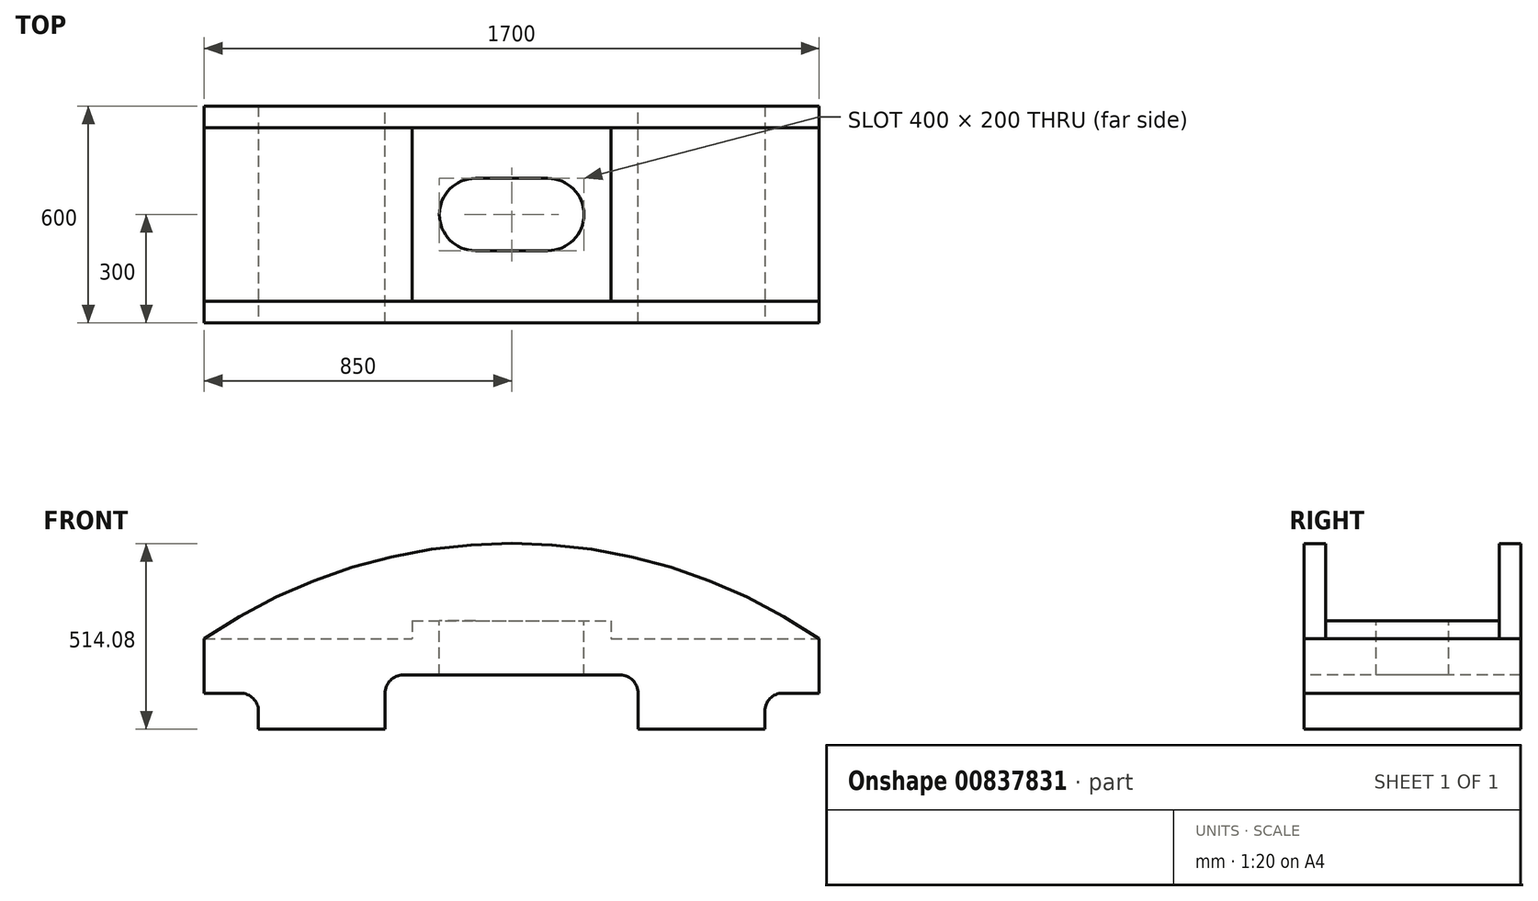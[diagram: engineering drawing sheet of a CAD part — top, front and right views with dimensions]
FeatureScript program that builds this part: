
annotation { "Feature Type Name" : "Feature", "Feature Type Description" : "" }
export const myFeature = defineFeature(function(context is Context, id is Id, definition is map)
    precondition{}
    {
        {
            var Q0;
            Q0=qCreatedBy(makeId("Front.planeOp"),FACE);
            var sketch = newSketch(context, id + "F0", { "sketchPlane" : qUnion([Q0])});
            skLineSegment(sketch, "E0.bottom", {"start": v(-850, -125) * mm, "end": v(850, -125) * mm});
            skLineSegment(sketch, "E0.top", {"start": v(-850, 125) * mm, "end": v(850, 125) * mm});
            skLineSegment(sketch, "E0.left", {"start": v(-850, -125) * mm, "end": v(-850, 125) * mm});
            skLineSegment(sketch, "E0.right", {"start": v(850, -125) * mm, "end": v(850, 125) * mm});
            skPoint(sketch, "E0.middle", {"position": v(0, 0) * mm});
            skSolve(sketch);
        }
        {
            var Q0;
            Q0 = qSketchRegion(id + "F0", true);
            var Q1;
            Q1 = qSketchRegion(id + "F2", true);
            extrude(context, id + "F1", {"entities" : qUnion([Q0, Q1]), "depth" : 600 * mm, "offsetDistance" : 25 * mm});
        }
        {
            var Q0;
            Q0=makeQuery(id+"F1.opExtrude","CAP_FACE",FACE,{"disambiguationData":[OSD([sQuery(id+"F0.wireOp",EDGE,"E0.bottom"),sQuery(id+"F0.wireOp",EDGE,"E0.top"),sQuery(id+"F0.wireOp",EDGE,"E0.left"),sQuery(id+"F0.wireOp",EDGE,"E0.right")])],"isStart":false});
            var sketch = newSketch(context, id + "F2", { "sketchPlane" : qUnion([Q0])});
            skLineSegment(sketch, "E1.bottom", {"start": v(-350, -275) * mm, "end": v(350, -275) * mm});
            skLineSegment(sketch, "E1.top", {"start": v(-350, 25) * mm, "end": v(350, 25) * mm});
            skLineSegment(sketch, "E1.left", {"start": v(-350, -275) * mm, "end": v(-350, 25) * mm});
            skLineSegment(sketch, "E1.right", {"start": v(350, -275) * mm, "end": v(350, 25) * mm});
            skPoint(sketch, "E1.middle", {"position": v(0, -125) * mm});
            skSolve(sketch);
        }
        {
            var Q0;
            Q0 = qSketchRegion(id + "F2", true);
            extrude(context, id + "F3", {"entities" : qUnion([Q0]), "operationType" : NewBodyOperationType.REMOVE, "endBound" : BoundingType.THROUGH_ALL, "oppositeDirection" : true, "depth" : 25 * mm, "offsetDistance" : 25 * mm});
        }
        {
            var Q0;
            Q0=makeQuery(id+"F1.opExtrude","CAP_FACE",FACE,{"disambiguationData":[OSD([sQuery(id+"F0.wireOp",EDGE,"E0.bottom"),sQuery(id+"F0.wireOp",EDGE,"E0.top"),sQuery(id+"F0.wireOp",EDGE,"E0.left"),sQuery(id+"F0.wireOp",EDGE,"E0.right")])],"isStart":false});
            var sketch = newSketch(context, id + "F4", { "sketchPlane" : qUnion([Q0])});
            skLineSegment(sketch, "E2.bottom", {"start": v(-850, -125) * mm, "end": v(-700, -125) * mm});
            skLineSegment(sketch, "E2.top", {"start": v(-850, -25) * mm, "end": v(-700, -25) * mm});
            skLineSegment(sketch, "E2.left", {"start": v(-850, -125) * mm, "end": v(-850, -25) * mm});
            skLineSegment(sketch, "E2.right", {"start": v(-700, -125) * mm, "end": v(-700, -25) * mm});
            skSolve(sketch);
        }
        {
            var Q0;
            Q0 = qSketchRegion(id + "F4", true);
            extrude(context, id + "F5", {"entities" : qUnion([Q0]), "operationType" : NewBodyOperationType.REMOVE, "endBound" : BoundingType.THROUGH_ALL, "oppositeDirection" : true, "depth" : 25 * mm, "offsetDistance" : 25 * mm});
        }
        {
            var Q0;
            Q0=makeQuery(id+"F1.opExtrude","CAP_FACE",FACE,{"disambiguationData":[OSD([sQuery(id+"F0.wireOp",EDGE,"E0.bottom"),sQuery(id+"F0.wireOp",EDGE,"E0.top"),sQuery(id+"F0.wireOp",EDGE,"E0.left"),sQuery(id+"F0.wireOp",EDGE,"E0.right")])],"isStart":false});
            var sketch = newSketch(context, id + "F6", { "sketchPlane" : qUnion([Q0])});
            skLineSegment(sketch, "E3.bottom", {"start": v(850, -125) * mm, "end": v(700, -125) * mm});
            skLineSegment(sketch, "E3.top", {"start": v(850, -25) * mm, "end": v(700, -25) * mm});
            skLineSegment(sketch, "E3.left", {"start": v(850, -125) * mm, "end": v(850, -25) * mm});
            skLineSegment(sketch, "E3.right", {"start": v(700, -125) * mm, "end": v(700, -25) * mm});
            skSolve(sketch);
        }
        {
            var Q0;
            Q0 = qSketchRegion(id + "F6", true);
            extrude(context, id + "F7", {"entities" : qUnion([Q0]), "operationType" : NewBodyOperationType.REMOVE, "endBound" : BoundingType.THROUGH_ALL, "oppositeDirection" : true, "depth" : 25 * mm, "offsetDistance" : 25 * mm});
        }
        {
            var Q0;
            Q0=makeQuery(id+"F1.opExtrude","CAP_FACE",FACE,{"disambiguationData":[OSD([sQuery(id+"F0.wireOp",EDGE,"E0.bottom"),sQuery(id+"F0.wireOp",EDGE,"E0.top"),sQuery(id+"F0.wireOp",EDGE,"E0.left"),sQuery(id+"F0.wireOp",EDGE,"E0.right")])],"isStart":false});
            var sketch = newSketch(context, id + "F8", { "sketchPlane" : qUnion([Q0])});
            skArc(sketch, "E4", {"start": v(850, 125) * mm, "mid": v(0, 389.08) * mm, "end": v(-850, 125) * mm});
            skSolve(sketch);
        }
        {
            var Q0;
            Q0 = qSketchRegion(id + "F8", true);
            var Q1;
            Q1=makeQuery(id+"F8.imprint","IMPRINT",FACE,{"disambiguationData":[TD([[makeQuery(id+"F8.imprint","IMPRINT",EDGE,{"derivedFrom":sQuery(id+"F8.wireOp",EDGE,"E4")}),1.0]])]});
            extrude(context, id + "F9", {"entities" : qUnion([Q0, Q1]), "operationType" : NewBodyOperationType.ADD, "oppositeDirection" : true, "depth" : 60 * mm, "offsetDistance" : 25 * mm});
        }
        {
            var Q0;
            Q0=makeQuery(id+"F1.opExtrude","CAP_FACE",FACE,{"disambiguationData":[OSD([sQuery(id+"F0.wireOp",EDGE,"E0.bottom"),sQuery(id+"F0.wireOp",EDGE,"E0.top"),sQuery(id+"F0.wireOp",EDGE,"E0.left"),sQuery(id+"F0.wireOp",EDGE,"E0.right")])],"isStart":true});
            var sketch = newSketch(context, id + "F10", { "sketchPlane" : qUnion([Q0])});
            skArc(sketch, "E5", {"start": v(850, 125) * mm, "mid": v(0, 389.08) * mm, "end": v(-850, 125) * mm});
            skSolve(sketch);
        }
        {
            var Q0;
            Q0 = qSketchRegion(id + "F10", true);
            var Q1;
            Q1=makeQuery(id+"F10.imprint","IMPRINT",FACE,{"disambiguationData":[TD([[makeQuery(id+"F10.imprint","IMPRINT",EDGE,{"derivedFrom":sQuery(id+"F10.wireOp",EDGE,"E5")}),1.0]])]});
            extrude(context, id + "F11", {"entities" : qUnion([Q0, Q1]), "operationType" : NewBodyOperationType.ADD, "oppositeDirection" : true, "depth" : 60 * mm, "offsetDistance" : 25 * mm});
        }
        {
            var Q0;
            Q0=makeQuery(id+"F1.opExtrude","SWEPT_FACE",FACE,{"disambiguationData":[OSD([sQuery(id+"F0.wireOp",EDGE,"E0.top")])]});
            var sketch = newSketch(context, id + "F12", { "sketchPlane" : qUnion([Q0])});
            skLineSegment(sketch, "E6.bottom", {"start": v(-275, -540) * mm, "end": v(275, -540) * mm});
            skLineSegment(sketch, "E6.top", {"start": v(-275, -60) * mm, "end": v(275, -60) * mm});
            skLineSegment(sketch, "E6.left", {"start": v(-275, -540) * mm, "end": v(-275, -60) * mm});
            skLineSegment(sketch, "E6.right", {"start": v(275, -540) * mm, "end": v(275, -60) * mm});
            skPoint(sketch, "E6.middle", {"position": v(0, -300) * mm});
            skPoint(sketch, "E6.middle.positionSnap0", {"position": v(-850, -300) * mm});
            skPoint(sketch, "E6.centerSnap0", {"position": v(-850, -300) * mm});
            skSolve(sketch);
        }
        {
            var Q0;
            Q0 = qSketchRegion(id + "F12", true);
            extrude(context, id + "F13", {"entities" : qUnion([Q0]), "operationType" : NewBodyOperationType.ADD, "depth" : 50 * mm, "offsetDistance" : 25 * mm});
        }
        {
            var Q0;
            Q0=makeQuery(id+"F13.opExtrude","CAP_FACE",FACE,{"disambiguationData":[OSD([sQuery(id+"F12.wireOp",EDGE,"E6.bottom"),sQuery(id+"F12.wireOp",EDGE,"E6.top"),sQuery(id+"F12.wireOp",EDGE,"E6.left"),sQuery(id+"F12.wireOp",EDGE,"E6.right")])],"isStart":false});
            var sketch = newSketch(context, id + "F14", { "sketchPlane" : qUnion([Q0])});
            skPoint(sketch, "E7.centerSnap0", {"position": v(-275, -300) * mm});
            skPoint(sketch, "E8.middle", {"position": v(0, -300) * mm});
            skLineSegment(sketch, "E9.bottom", {"start": v(-100, -400) * mm, "end": v(100, -400) * mm});
            skLineSegment(sketch, "E9.top", {"start": v(-100, -200) * mm, "end": v(100, -200) * mm});
            skArc(sketch, "E10", {"start": v(-100, -200) * mm, "mid": v(-200, -300) * mm, "end": v(-100, -400) * mm});
            skArc(sketch, "E11", {"start": v(100, -400) * mm, "mid": v(200, -300) * mm, "end": v(100, -200) * mm});
            skSolve(sketch);
        }
        {
            var Q0;
            Q0 = qSketchRegion(id + "F14", true);
            extrude(context, id + "F15", {"entities" : qUnion([Q0]), "operationType" : NewBodyOperationType.REMOVE, "endBound" : BoundingType.THROUGH_ALL, "oppositeDirection" : true, "depth" : 25 * mm, "offsetDistance" : 25 * mm});
        }
        {
            var Q0;
            Q0=makeQuery(id+"F5.boolean.opBoolean","COPY",EDGE,{"derivedFrom":makeQuery(id+"F5.opExtrude","SWEPT_EDGE",EDGE,{"disambiguationData":[OSD([sQuery(id+"F4.wireOp",EDGE,"E2.top"),sQuery(id+"F4.wireOp",EDGE,"E2.right")])]})});
            fillet(context, id + "F16", {"entities" : qUnion([Q0]), "radius" : 50 * mm, "tangentPropagation" : true, "allowEdgeOverflow" : false});
        }
        {
            var Q0;
            Q0=makeQuery(id+"F3.boolean.opBoolean","COPY",EDGE,{"derivedFrom":makeQuery(id+"F3.opExtrude","SWEPT_EDGE",EDGE,{"disambiguationData":[OSD([sQuery(id+"F2.wireOp",EDGE,"E1.top"),sQuery(id+"F2.wireOp",EDGE,"E1.left")])]})});
            fillet(context, id + "F17", {"entities" : qUnion([Q0]), "radius" : 50 * mm, "tangentPropagation" : true, "allowEdgeOverflow" : false});
        }
        {
            var Q0;
            Q0=makeQuery(id+"F3.boolean.opBoolean","COPY",EDGE,{"derivedFrom":makeQuery(id+"F3.opExtrude","SWEPT_EDGE",EDGE,{"disambiguationData":[OSD([sQuery(id+"F2.wireOp",EDGE,"E1.top"),sQuery(id+"F2.wireOp",EDGE,"E1.right")])]})});
            fillet(context, id + "F18", {"entities" : qUnion([Q0]), "radius" : 50 * mm, "tangentPropagation" : true, "allowEdgeOverflow" : false});
        }
        {
            var Q0;
            Q0=makeQuery(id+"F7.boolean.opBoolean","COPY",EDGE,{"derivedFrom":makeQuery(id+"F7.opExtrude","SWEPT_EDGE",EDGE,{"disambiguationData":[OSD([sQuery(id+"F6.wireOp",EDGE,"E3.top"),sQuery(id+"F6.wireOp",EDGE,"E3.right")])]})});
            fillet(context, id + "F19", {"entities" : qUnion([Q0]), "radius" : 50 * mm, "tangentPropagation" : true, "allowEdgeOverflow" : false});
        }
        {
            var Q0;
            Q0 = qSketchRegion(id + "F14", true);
            extrude(context, id + "F20", {"entities" : qUnion([Q0]), "operationType" : NewBodyOperationType.REMOVE, "endBound" : BoundingType.THROUGH_ALL, "oppositeDirection" : true, "depth" : 25 * mm, "offsetDistance" : 25 * mm});
        }
    });
